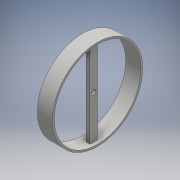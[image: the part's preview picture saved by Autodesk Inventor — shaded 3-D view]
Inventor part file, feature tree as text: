
AUTODESK INVENTOR PART (.ipt)
format: ipt  version: 2016 (Build 200138000, 138)  size: 118,784 bytes
history: native  units: mm
features: extrude x2, sketch x2, other x1
ambient origin geometry x8: Origin, YZ Plane, XZ Plane, XY Plane, X Axis, Y Axis, Z Axis, Center Point
bodies: Body1 (feature_tree)
feature tree (5):
  other  "Sólido1"
  extrude  "Extrusión1"  Depth=4.0mm
  extrude  "Extrusión2"  Depth=23.0mm
  sketch  "Boceto1"  dims[d0=4.0mm d1=46.0mm]
  sketch  "Boceto2"  dims[d2=2.0mm d3=23.0mm d4=2.5mm d5=2.0mm d6=0.0mm d7=48.0mm d8=46.0mm d9=8.0mm d10=0.0mm]
